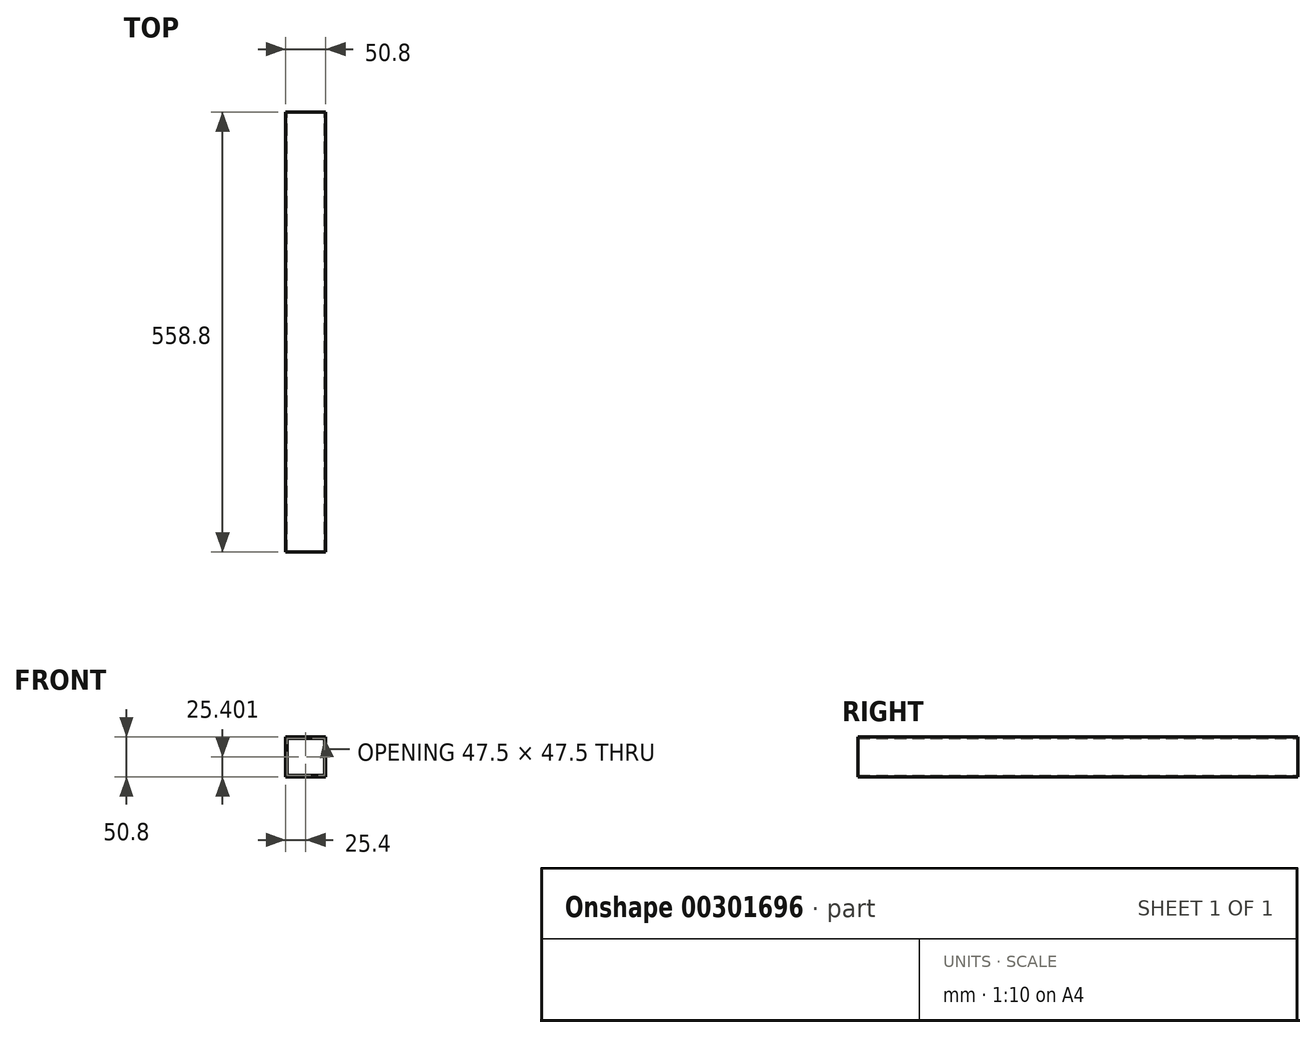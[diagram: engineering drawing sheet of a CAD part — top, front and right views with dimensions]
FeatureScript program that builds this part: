
annotation { "Feature Type Name" : "Feature", "Feature Type Description" : "" }
export const myFeature = defineFeature(function(context is Context, id is Id, definition is map)
    precondition{}
    {
        {
            var Q0;
            Q0=qCreatedBy(makeId("Front.planeOp"),FACE);
            var sketch = newSketch(context, id + "F0", { "sketchPlane" : qUnion([Q0])});
            skLineSegment(sketch, "E0.bottom", {"start": v(25.4, -27.25) * mm, "end": v(-25.4, -27.25) * mm});
            skLineSegment(sketch, "E0.top", {"start": v(25.4, 23.55) * mm, "end": v(-25.4, 23.55) * mm});
            skLineSegment(sketch, "E0.left", {"start": v(25.4, -27.25) * mm, "end": v(25.4, 23.55) * mm});
            skLineSegment(sketch, "E0.right", {"start": v(-25.4, -27.25) * mm, "end": v(-25.4, 23.55) * mm});
            skPoint(sketch, "E0.middle", {"position": v(0, -1.85) * mm});
            skLineSegment(sketch, "E1.0", {"start": v(22.1, 21.9) * mm, "end": v(-22.1, 21.9) * mm});
            skLineSegment(sketch, "E1.1", {"start": v(23.75, -23.95) * mm, "end": v(23.75, 20.25) * mm});
            skLineSegment(sketch, "E1.2", {"start": v(22.1, -25.6) * mm, "end": v(-22.1, -25.6) * mm});
            skLineSegment(sketch, "E1.3", {"start": v(-23.75, -23.95) * mm, "end": v(-23.75, 20.25) * mm});
            skPoint(sketch, "E2.visualSharp", {"position": v(-23.75, 21.9) * mm});
            skArc(sketch, "E2.filletArc", {"start": v(-22.1, 21.9) * mm, "mid": v(-23.27, 21.42) * mm, "end": v(-23.75, 20.25) * mm});
            skPoint(sketch, "E3.visualSharp", {"position": v(23.75, 21.9) * mm});
            skArc(sketch, "E3.filletArc", {"start": v(23.75, 20.25) * mm, "mid": v(23.27, 21.42) * mm, "end": v(22.1, 21.9) * mm});
            skPoint(sketch, "E4.visualSharp", {"position": v(23.75, -25.6) * mm});
            skArc(sketch, "E4.filletArc", {"start": v(22.1, -25.6) * mm, "mid": v(23.27, -25.11) * mm, "end": v(23.75, -23.95) * mm});
            skPoint(sketch, "E5.visualSharp", {"position": v(-23.75, -25.6) * mm});
            skArc(sketch, "E5.filletArc", {"start": v(-23.75, -23.95) * mm, "mid": v(-23.27, -25.11) * mm, "end": v(-22.1, -25.6) * mm});
            skSolve(sketch);
        }
        {
            var Q0;
            Q0=makeQuery(id+"F0.imprint","IMPRINT",FACE,{"disambiguationData":[TD([[makeQuery(id+"F0.imprint","IMPRINT",EDGE,{"derivedFrom":sQuery(id+"F0.wireOp",EDGE,"E0.bottom")}),-1.0]])]});
            extrude(context, id + "F1", {"entities" : qUnion([Q0]), "depth" : 558.8 * mm});
        }
    });
